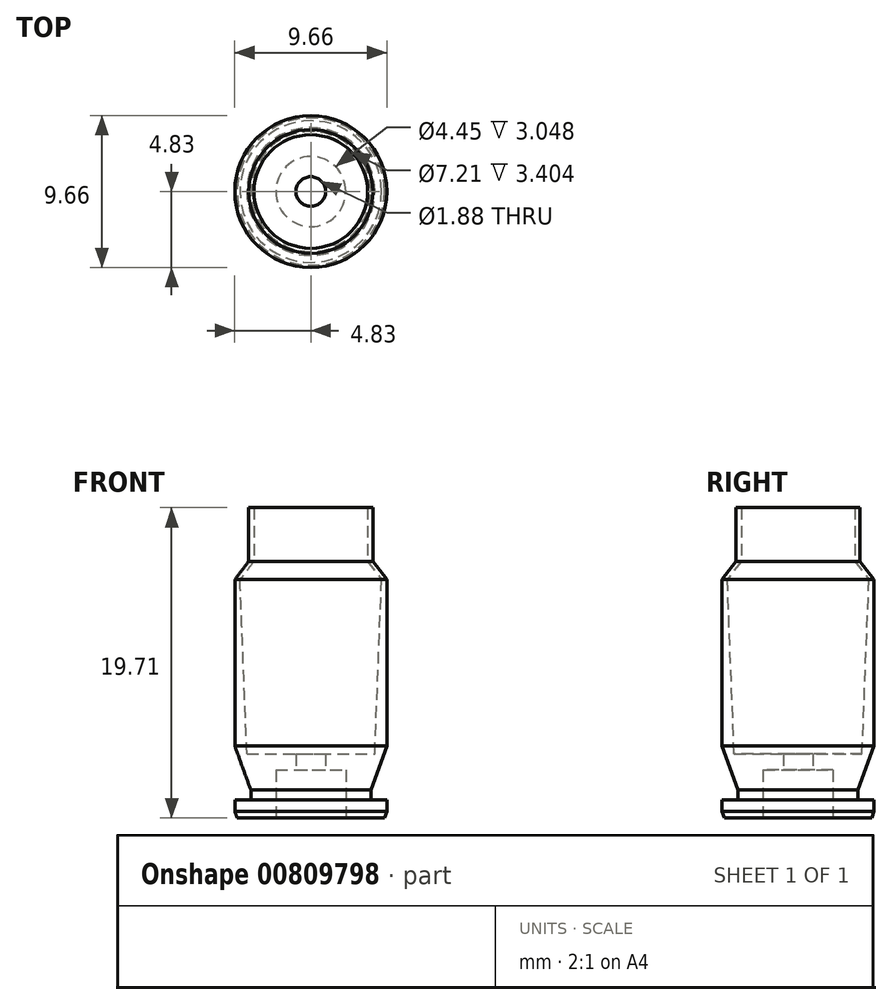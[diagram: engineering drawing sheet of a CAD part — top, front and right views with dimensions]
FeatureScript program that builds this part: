
annotation { "Feature Type Name" : "Feature", "Feature Type Description" : "" }
export const myFeature = defineFeature(function(context is Context, id is Id, definition is map)
    precondition{}
    {
        {
            var Q0;
            Q0=qCreatedBy(makeId("Front.planeOp"),FACE);
            var sketch = newSketch(context, id + "F0", { "sketchPlane" : qUnion([Q0])});
            skLineSegment(sketch, "E0", {"start": v(2.22, 0) * mm, "end": v(4.68, 0) * mm});
            skLineSegment(sketch, "E1", {"start": v(4.83, 0.4) * mm, "end": v(4.83, 1.14) * mm});
            skLineSegment(sketch, "E2", {"start": v(4.83, 1.14) * mm, "end": v(3.81, 1.14) * mm});
            skLineSegment(sketch, "E3", {"start": v(4.83, 4.57) * mm, "end": v(4.83, 15.14) * mm});
            skLineSegment(sketch, "E4", {"start": v(4.83, 15.14) * mm, "end": v(3.94, 16.3) * mm});
            skLineSegment(sketch, "E5", {"start": v(3.94, 16.3) * mm, "end": v(3.94, 19.71) * mm});
            skLineSegment(sketch, "E6", {"start": v(3.94, 19.71) * mm, "end": v(3.6, 19.71) * mm});
            skLineSegment(sketch, "E7", {"start": v(3.6, 19.71) * mm, "end": v(3.6, 16.3) * mm});
            skLineSegment(sketch, "E8", {"start": v(3.6, 16.3) * mm, "end": v(4.5, 15.14) * mm});
            skLineSegment(sketch, "E9", {"start": v(0.94, 4.06) * mm, "end": v(0.94, 3.05) * mm});
            skLineSegment(sketch, "E10", {"start": v(0.94, 3.05) * mm, "end": v(2.22, 3.05) * mm});
            skLineSegment(sketch, "E11", {"start": v(2.22, 3.05) * mm, "end": v(2.22, 0) * mm});
            skLineSegment(sketch, "E12", {"start": v(3.81, 1.14) * mm, "end": v(3.81, 1.78) * mm});
            skLineSegment(sketch, "E13", {"start": v(3.81, 1.78) * mm, "end": v(4.83, 4.57) * mm});
            skPoint(sketch, "E14.orphan", {"position": v(4.45, 4.57) * mm});
            skLineSegment(sketch, "E15", {"start": v(4.83, 0.4) * mm, "end": v(4.68, 0) * mm});
            skPoint(sketch, "E16.orphan", {"position": v(4.83, 0) * mm});
            skLineSegment(sketch, "E17", {"start": v(0, 0) * mm, "end": v(0, 23) * mm});
            skPoint(sketch, "E18.end.orphan", {"position": v(4.44, 3.8) * mm});
            skLineSegment(sketch, "E19", {"start": v(0.94, 4.06) * mm, "end": v(4.06, 4.06) * mm});
            skLineSegment(sketch, "E20", {"start": v(4.06, 4.06) * mm, "end": v(4.5, 15.14) * mm});
            skSolve(sketch);
        }
        {
            var Q0;
            Q0=qSketchRegion(id+"F0",true);
            var Q1;
            Q1=sQuery(id+"F0.wireOp",EDGE,"E17");
            revolve(context, id + "F1", {"surfaceOperationType" : NewSurfaceOperationType.NEW, "entities" : qUnion([Q0]), "axis" : qUnion([Q1]), "revolveType" : RevolveType.FULL});
        }
        {
            var Q0;
            Q0=makeQuery(id+"F1.opRevolve","SWEPT_BODY",BODY,{"disambiguationData":[OSD([sQuery(id+"F0.wireOp",EDGE,"E0"),sQuery(id+"F0.wireOp",EDGE,"E1"),sQuery(id+"F0.wireOp",EDGE,"E2"),sQuery(id+"F0.wireOp",EDGE,"E3"),sQuery(id+"F0.wireOp",EDGE,"E4"),sQuery(id+"F0.wireOp",EDGE,"E5"),sQuery(id+"F0.wireOp",EDGE,"E6"),sQuery(id+"F0.wireOp",EDGE,"E7"),sQuery(id+"F0.wireOp",EDGE,"E8"),sQuery(id+"F0.wireOp",EDGE,"1Kn2wOzD-5aWn-3HVJ-gkRw-BWBTK5LSjuYW"),sQuery(id+"F0.wireOp",EDGE,"E9"),sQuery(id+"F0.wireOp",EDGE,"E10"),sQuery(id+"F0.wireOp",EDGE,"E11"),sQuery(id+"F0.wireOp",EDGE,"E12"),sQuery(id+"F0.wireOp",EDGE,"E13"),sQuery(id+"F0.wireOp",EDGE,"E18"),sQuery(id+"F0.wireOp",EDGE,"E15")])]});
            transform(context, id + "F2", {"entities" : qUnion([Q0]), "transformType" : TransformType.TRANSLATION_3D, "dx" : 0 * mm, "dy" : 0 * mm, "dz" : 0 * mm, "makeCopy" : true});
        }
        {
            var Q0;
            Q0=makeQuery(id+"F2.opPattern","COPY",BODY,{"derivedFrom":makeQuery(id+"F1.opRevolve","SWEPT_BODY",BODY,{"disambiguationData":[OSD([sQuery(id+"F0.wireOp",EDGE,"E0"),sQuery(id+"F0.wireOp",EDGE,"E1"),sQuery(id+"F0.wireOp",EDGE,"E2"),sQuery(id+"F0.wireOp",EDGE,"E3"),sQuery(id+"F0.wireOp",EDGE,"E4"),sQuery(id+"F0.wireOp",EDGE,"E5"),sQuery(id+"F0.wireOp",EDGE,"E6"),sQuery(id+"F0.wireOp",EDGE,"E7"),sQuery(id+"F0.wireOp",EDGE,"E8"),sQuery(id+"F0.wireOp",EDGE,"1Kn2wOzD-5aWn-3HVJ-gkRw-BWBTK5LSjuYW"),sQuery(id+"F0.wireOp",EDGE,"E9"),sQuery(id+"F0.wireOp",EDGE,"E10"),sQuery(id+"F0.wireOp",EDGE,"E11"),sQuery(id+"F0.wireOp",EDGE,"E12"),sQuery(id+"F0.wireOp",EDGE,"E13"),sQuery(id+"F0.wireOp",EDGE,"E18"),sQuery(id+"F0.wireOp",EDGE,"E15")])]}),"instanceName":"1"});
            deleteBodies(context, id + "F3", {"entities" : qUnion([Q0])});
        }
    });
